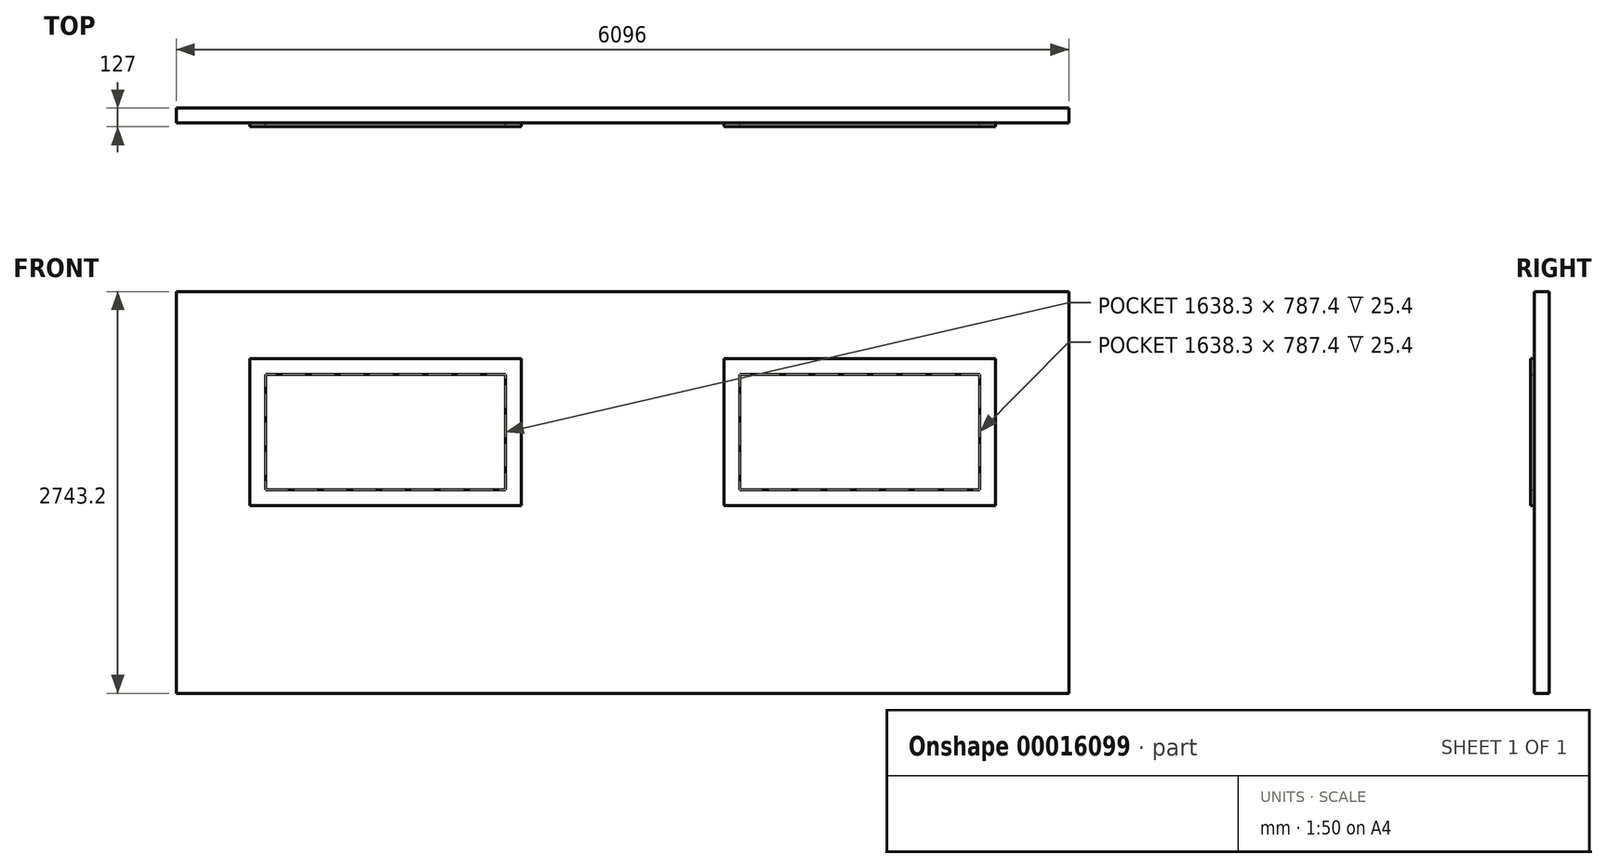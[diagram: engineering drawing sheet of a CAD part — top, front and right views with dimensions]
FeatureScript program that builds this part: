
annotation { "Feature Type Name" : "Feature", "Feature Type Description" : "" }
export const myFeature = defineFeature(function(context is Context, id is Id, definition is map)
    precondition{}
    {
        {
            var Q0;
            Q0=qCreatedBy(makeId("Front.planeOp"),FACE);
            var sketch = newSketch(context, id + "F0", { "sketchPlane" : qUnion([Q0])});
            skLineSegment(sketch, "E0.rect.bottom", {"start": v(3048, 1371.6) * mm, "end": v(-3048, 1371.6) * mm});
            skLineSegment(sketch, "E0.rect.top", {"start": v(3048, -1371.6) * mm, "end": v(-3048, -1371.6) * mm});
            skLineSegment(sketch, "E0.rect.left", {"start": v(3048, 1371.6) * mm, "end": v(3048, -1371.6) * mm});
            skLineSegment(sketch, "E0.rect.right", {"start": v(-3048, 1371.6) * mm, "end": v(-3048, -1371.6) * mm});
            skPoint(sketch, "E0.rect.middle", {"position": v(0, 0) * mm});
            skSolve(sketch);
        }
        {
            var Q0;
            Q0=makeQuery(id+"F0.imprint","IMPRINT",FACE,{"disambiguationData":[TD([[makeQuery(id+"F0.imprint","IMPRINT",EDGE,{"derivedFrom":sQuery(id+"F0.wireOp",EDGE,"E0.rect.bottom")}),1.0]])]});
            extrude(context, id + "F1", {"entities" : qUnion([Q0]), "depth" : 101.6 * mm});
        }
        {
            var Q0;
            Q0=makeQuery(id+"F1.opExtrude","CAP_FACE",FACE,{"disambiguationData":[OSD([sQuery(id+"F0.wireOp",EDGE,"E0.rect.bottom"),sQuery(id+"F0.wireOp",EDGE,"E0.rect.top"),sQuery(id+"F0.wireOp",EDGE,"E0.rect.left"),sQuery(id+"F0.wireOp",EDGE,"E0.rect.right")])],"isStart":false});
            var sketch = newSketch(context, id + "F2", { "sketchPlane" : qUnion([Q0])});
            skLineSegment(sketch, "E1.rect.bottom", {"start": v(-692.15, 914.4) * mm, "end": v(-2546.35, 914.4) * mm});
            skLineSegment(sketch, "E1.rect.top", {"start": v(-692.15, -88.9) * mm, "end": v(-2546.35, -88.9) * mm});
            skLineSegment(sketch, "E1.rect.left", {"start": v(-692.15, 914.4) * mm, "end": v(-692.15, -88.9) * mm});
            skLineSegment(sketch, "E1.rect.right", {"start": v(-2546.35, 914.4) * mm, "end": v(-2546.35, -88.9) * mm});
            skPoint(sketch, "E1.rect.middle", {"position": v(-1619.25, 412.75) * mm});
            skLineSegment(sketch, "E2.rect.bottom", {"start": v(2546.35, 914.4) * mm, "end": v(692.15, 914.4) * mm});
            skLineSegment(sketch, "E2.rect.top", {"start": v(2546.35, -88.9) * mm, "end": v(692.15, -88.9) * mm});
            skLineSegment(sketch, "E2.rect.left", {"start": v(2546.35, 914.4) * mm, "end": v(2546.35, -88.9) * mm});
            skLineSegment(sketch, "E2.rect.right", {"start": v(692.15, 914.4) * mm, "end": v(692.15, -88.9) * mm});
            skPoint(sketch, "E2.rect.middle", {"position": v(1619.25, 412.75) * mm});
            skLineSegment(sketch, "E3", {"start": v(-1619.25, 412.75) * mm, "end": v(1619.25, 412.75) * mm, "construction": true});
            skLineSegment(sketch, "E4.rect.bottom", {"start": v(-800.1, 806.45) * mm, "end": v(-2438.4, 806.45) * mm});
            skLineSegment(sketch, "E4.rect.top", {"start": v(-800.1, 19.05) * mm, "end": v(-2438.4, 19.05) * mm});
            skLineSegment(sketch, "E4.rect.left", {"start": v(-800.1, 806.45) * mm, "end": v(-800.1, 19.05) * mm});
            skLineSegment(sketch, "E4.rect.right", {"start": v(-2438.4, 806.45) * mm, "end": v(-2438.4, 19.05) * mm});
            skLineSegment(sketch, "E5", {"start": v(0, 0) * mm, "end": v(0, 412.75) * mm, "construction": true});
            skLineSegment(sketch, "E6.rect.bottom", {"start": v(2438.4, 806.45) * mm, "end": v(800.1, 806.45) * mm});
            skLineSegment(sketch, "E6.rect.top", {"start": v(2438.4, 19.05) * mm, "end": v(800.1, 19.05) * mm});
            skLineSegment(sketch, "E6.rect.left", {"start": v(2438.4, 806.45) * mm, "end": v(2438.4, 19.05) * mm});
            skLineSegment(sketch, "E6.rect.right", {"start": v(800.1, 806.45) * mm, "end": v(800.1, 19.05) * mm});
            skSolve(sketch);
        }
        {
            var Q0;
            Q0=makeQuery(id+"F2.imprint","IMPRINT",FACE,{"disambiguationData":[TD([[makeQuery(id+"F2.imprint","IMPRINT",EDGE,{"derivedFrom":sQuery(id+"F2.wireOp",EDGE,"E1.rect.bottom")}),1.0]])]});
            var Q1;
            Q1=makeQuery(id+"F2.imprint","IMPRINT",FACE,{"disambiguationData":[TD([[makeQuery(id+"F2.imprint","IMPRINT",EDGE,{"derivedFrom":sQuery(id+"F2.wireOp",EDGE,"E2.rect.bottom")}),1.0]])]});
            extrude(context, id + "F3", {"entities" : qUnion([Q0, Q1]), "operationType" : NewBodyOperationType.ADD, "depth" : 25.4 * mm});
        }
    });
